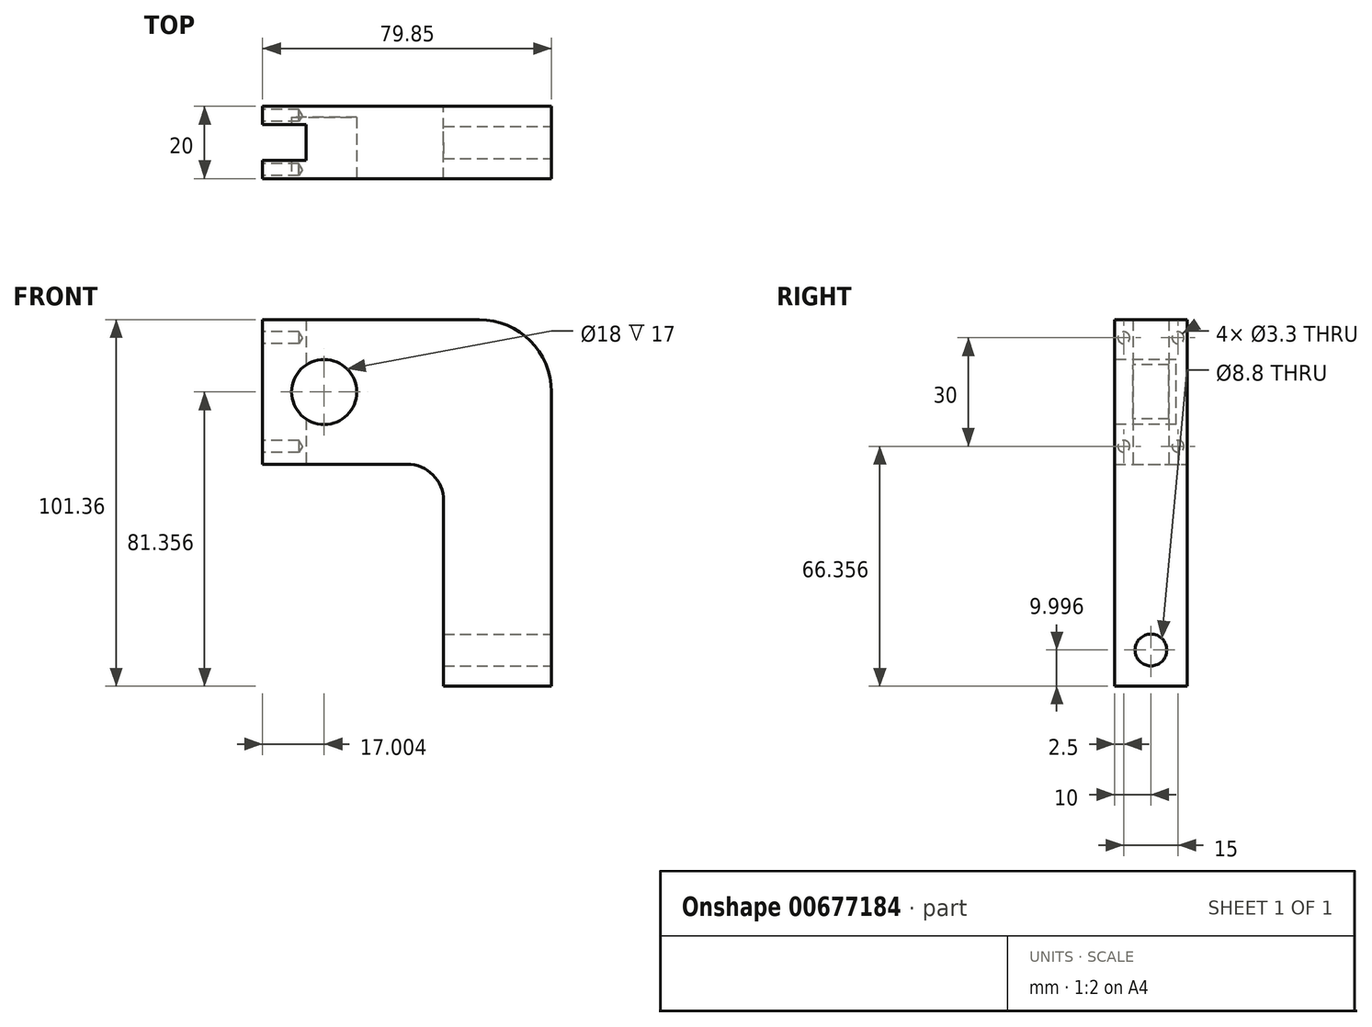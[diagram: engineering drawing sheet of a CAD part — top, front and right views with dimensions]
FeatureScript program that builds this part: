
annotation { "Feature Type Name" : "Feature", "Feature Type Description" : "" }
export const myFeature = defineFeature(function(context is Context, id is Id, definition is map)
    precondition{}
    {
        {
            var Q0;
            Q0=qCreatedBy(makeId("Front.planeOp"),FACE);
            var sketch = newSketch(context, id + "F0", { "sketchPlane" : qUnion([Q0])});
            skLineSegment(sketch, "E0", {"start": v(-40.38, 44.54) * mm, "end": v(39.47, 44.54) * mm});
            skLineSegment(sketch, "E1", {"start": v(39.47, 44.54) * mm, "end": v(39.47, -56.82) * mm});
            skLineSegment(sketch, "E2", {"start": v(39.47, -56.82) * mm, "end": v(9.62, -56.82) * mm});
            skLineSegment(sketch, "E3", {"start": v(9.62, -56.82) * mm, "end": v(9.62, 4.54) * mm});
            skLineSegment(sketch, "E4", {"start": v(9.62, 4.54) * mm, "end": v(-40.38, 4.54) * mm});
            skLineSegment(sketch, "E5", {"start": v(-40.38, 4.54) * mm, "end": v(-40.38, 44.54) * mm});
            skSolve(sketch);
        }
        {
            var Q0;
            Q0 = qSketchRegion(id + "F0", true);
            extrude(context, id + "F1", {"entities" : qUnion([Q0]), "depth" : 20 * mm, "offsetDistance" : 25 * mm});
        }
        {
            var Q0;
            Q0=makeQuery(id+"F1.opExtrude","SWEPT_EDGE",EDGE,{"disambiguationData":[OSD([sQuery(id+"F0.wireOp",EDGE,"E3"),sQuery(id+"F0.wireOp",EDGE,"E4")])]});
            fillet(context, id + "F2", {"entities" : qUnion([Q0]), "radius" : 10 * mm, "tangentPropagation" : true, "allowEdgeOverflow" : false});
        }
        {
            var Q0;
            Q0=makeQuery(id+"F1.opExtrude","SWEPT_EDGE",EDGE,{"disambiguationData":[OSD([sQuery(id+"F0.wireOp",EDGE,"E0"),sQuery(id+"F0.wireOp",EDGE,"E1")])]});
            fillet(context, id + "F3", {"entities" : qUnion([Q0]), "radius" : 20 * mm, "tangentPropagation" : true, "allowEdgeOverflow" : false});
        }
        {
            var Q0;
            Q0=makeQuery(id+"F1.opExtrude","SWEPT_FACE",FACE,{"disambiguationData":[OSD([sQuery(id+"F0.wireOp",EDGE,"E1")])]});
            var sketch = newSketch(context, id + "F4", { "sketchPlane" : qUnion([Q0])});
            skPoint(sketch, "E6", {"position": v(-10, -46.82) * mm});
            skSolve(sketch);
        }
        {
            var Q0;
            Q0=sQuery(id+"F4.wireOp",VERTEX,"E6");
            var Q1;
            Q1=makeQuery(id+"F1.opExtrude","SWEPT_BODY",BODY,{"disambiguationData":[OSD([sQuery(id+"F0.wireOp",EDGE,"E0"),sQuery(id+"F0.wireOp",EDGE,"E1"),sQuery(id+"F0.wireOp",EDGE,"E2"),sQuery(id+"F0.wireOp",EDGE,"E3"),sQuery(id+"F0.wireOp",EDGE,"E4"),sQuery(id+"F0.wireOp",EDGE,"E5")])]});
            hole(context, id + "F5", {"style" : HoleStyle.SIMPLE, "endStyle" : HoleEndStyle.THROUGH, "standardTappedOrClearance" : lookupTablePath({ "standard" : "ISO", "fit" : "Normal", "size" : "M8", "type" : "Clearance" }), "standardBlindInLast" : lookupTablePath({ "fit" : "Standard", "standard" : "ISO", "size" : "M8", "type" : "Clearance" }), "holeDiameter" : 8.8 * mm, "majorDiameter" : 5 * mm, "isTappedThrough" : true, "tappedDepth" : 12 * mm, "tapClearance" : 3, "locations" : qUnion([Q0]), "scope" : qUnion([Q1])});
        }
        {
            var Q0;
            Q0=makeQuery(id+"F1.opExtrude","SWEPT_FACE",FACE,{"disambiguationData":[OSD([sQuery(id+"F0.wireOp",EDGE,"E5")])]});
            var sketch = newSketch(context, id + "F6", { "sketchPlane" : qUnion([Q0])});
            skLineSegment(sketch, "E7.bottom", {"start": v(5, 44.54) * mm, "end": v(15, 44.54) * mm});
            skLineSegment(sketch, "E7.top", {"start": v(5, 4.54) * mm, "end": v(15, 4.54) * mm});
            skLineSegment(sketch, "E7.left", {"start": v(5, 44.54) * mm, "end": v(5, 4.54) * mm});
            skLineSegment(sketch, "E7.right", {"start": v(15, 44.54) * mm, "end": v(15, 4.54) * mm});
            skSolve(sketch);
        }
        {
            var Q0;
            Q0 = qSketchRegion(id + "F6", true);
            extrude(context, id + "F7", {"entities" : qUnion([Q0]), "operationType" : NewBodyOperationType.REMOVE, "oppositeDirection" : true, "depth" : 12 * mm, "offsetDistance" : 25 * mm});
        }
        {
            var Q0;
            Q0=makeQuery(id+"F1.opExtrude","CAP_FACE",FACE,{"disambiguationData":[OSD([sQuery(id+"F0.wireOp",EDGE,"E0"),sQuery(id+"F0.wireOp",EDGE,"E1"),sQuery(id+"F0.wireOp",EDGE,"E2"),sQuery(id+"F0.wireOp",EDGE,"E3"),sQuery(id+"F0.wireOp",EDGE,"E4"),sQuery(id+"F0.wireOp",EDGE,"E5")])],"isStart":false});
            var sketch = newSketch(context, id + "F8", { "sketchPlane" : qUnion([Q0])});
            skCircle(sketch, "E8", {"center": v(-23.38, 24.54) * mm, "radius": 9 * mm});
            skPoint(sketch, "E8.centerSnap0", {"position": v(-40.38, 24.54) * mm});
            skSolve(sketch);
        }
        {
            var Q0;
            Q0 = qSketchRegion(id + "F8", true);
            extrude(context, id + "F9", {"entities" : qUnion([Q0]), "operationType" : NewBodyOperationType.REMOVE, "oppositeDirection" : true, "depth" : 17 * mm, "offsetDistance" : 25 * mm});
        }
        {
            var Q0;
            {var subQ1=sQuery(id+"F0.wireOp",EDGE,"E5");Q0=makeQuery(id+"F7.boolean.opBoolean","SPLIT",FACE,{"disambiguationData":[TD([makeQuery(id+"F7.opExtrude","SWEPT_FACE",FACE,{"disambiguationData":[OSD([sQuery(id+"F6.wireOp",EDGE,"E7.left")])]})])],"derivedFrom":makeQuery(id+"F1.opExtrude","SWEPT_FACE",FACE,{"disambiguationData":[OSD([subQ1])]})});}
            var sketch = newSketch(context, id + "F10", { "sketchPlane" : qUnion([Q0])});
            skPoint(sketch, "E9", {"position": v(2.5, 39.54) * mm});
            skPoint(sketch, "E10", {"position": v(17.5, 39.54) * mm});
            skPoint(sketch, "E11", {"position": v(17.5, 9.54) * mm});
            skPoint(sketch, "E12", {"position": v(2.5, 9.54) * mm});
            skSolve(sketch);
        }
        {
            var Q0;
            Q0=sQuery(id+"F10.wireOp",VERTEX,"E9");
            var Q1;
            Q1=sQuery(id+"F10.wireOp",VERTEX,"E10");
            var Q2;
            Q2=sQuery(id+"F10.wireOp",VERTEX,"E11");
            var Q3;
            Q3=sQuery(id+"F10.wireOp",VERTEX,"E12");
            var Q4;
            Q4=makeQuery(id+"F1.opExtrude","SWEPT_BODY",BODY,{"disambiguationData":[OSD([sQuery(id+"F0.wireOp",EDGE,"E0"),sQuery(id+"F0.wireOp",EDGE,"E1"),sQuery(id+"F0.wireOp",EDGE,"E2"),sQuery(id+"F0.wireOp",EDGE,"E3"),sQuery(id+"F0.wireOp",EDGE,"E4"),sQuery(id+"F0.wireOp",EDGE,"E5")])]});
            hole(context, id + "F11", {"style" : HoleStyle.SIMPLE, "endStyle" : HoleEndStyle.BLIND, "standardTappedOrClearance" : lookupTablePath({ "standard" : "ISO", "fit" : "Normal", "size" : "M3", "type" : "Clearance" }), "standardBlindInLast" : lookupTablePath({ "fit" : "Standard", "standard" : "ISO", "size" : "M3", "type" : "Clearance" }), "holeDiameter" : 3.3 * mm, "majorDiameter" : 5 * mm, "holeDepth" : 10 * mm, "isTappedThrough" : true, "tappedDepth" : 12 * mm, "tapClearance" : 3, "locations" : qUnion([Q0, Q1, Q2, Q3]), "scope" : qUnion([Q4])});
        }
    });
